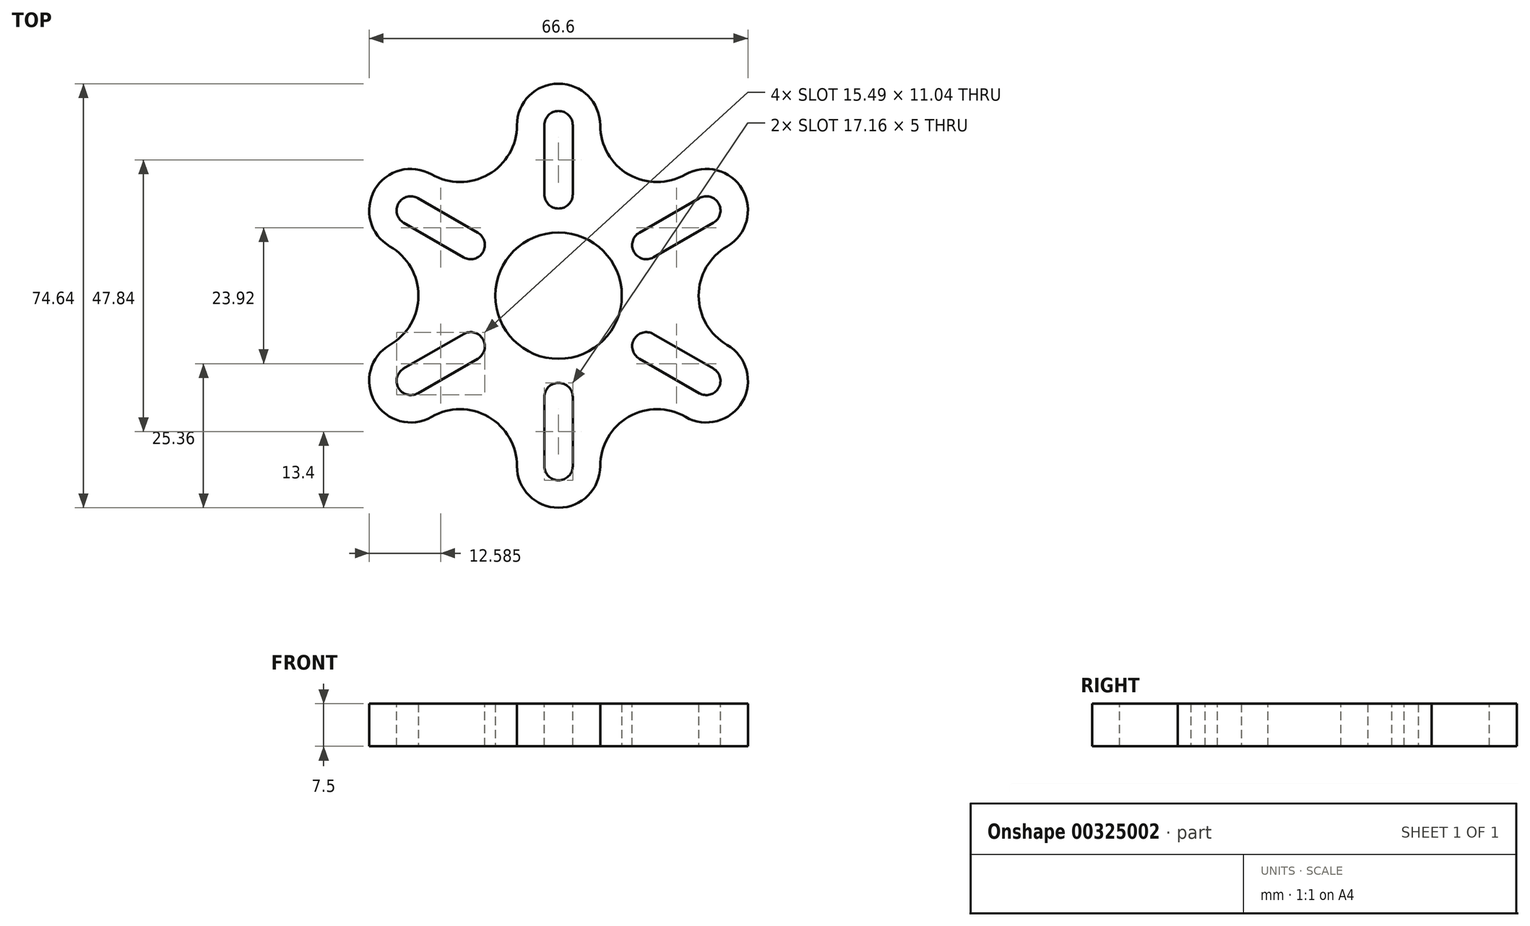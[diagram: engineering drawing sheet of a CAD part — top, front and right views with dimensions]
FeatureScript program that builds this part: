
annotation { "Feature Type Name" : "Feature", "Feature Type Description" : "" }
export const myFeature = defineFeature(function(context is Context, id is Id, definition is map)
    precondition{}
    {
        {
            var Q0;
            Q0=qCreatedBy(makeId("Top.planeOp"),FACE);
            var sketch = newSketch(context, id + "F0", { "sketchPlane" : qUnion([Q0])});
            skCircle(sketch, "E0", {"center": v(0, 0) * mm, "radius": 11.12 * mm});
            skPoint(sketch, "E1", {"position": v(0, 30) * mm});
            skCircle(sketch, "E2.cCircle", {"center": v(0, 0) * mm, "radius": 30 * mm, "construction": true});
            skLineSegment(sketch, "E2.0", {"start": v(-17.32, 30) * mm, "end": v(17.32, 30) * mm});
            skLineSegment(sketch, "E2.1", {"start": v(17.32, 30) * mm, "end": v(34.64, 0) * mm});
            skLineSegment(sketch, "E2.2", {"start": v(34.64, 0) * mm, "end": v(17.32, -30) * mm});
            skLineSegment(sketch, "E2.3", {"start": v(17.32, -30) * mm, "end": v(-17.32, -30) * mm});
            skLineSegment(sketch, "E2.4", {"start": v(-17.32, -30) * mm, "end": v(-34.64, 0) * mm});
            skLineSegment(sketch, "E2.5", {"start": v(-34.64, 0) * mm, "end": v(-17.32, 30) * mm});
            skPoint(sketch, "E3", {"position": v(-25.98, -15) * mm});
            skPoint(sketch, "E4", {"position": v(-25.98, 15) * mm});
            skPoint(sketch, "E5", {"position": v(25.98, 15) * mm});
            skPoint(sketch, "E6", {"position": v(25.98, -15) * mm});
            skCircle(sketch, "E7", {"center": v(-17.32, 30) * mm, "radius": 10 * mm});
            skCircle(sketch, "E8", {"center": v(-34.64, 0) * mm, "radius": 10 * mm});
            skCircle(sketch, "E9", {"center": v(-17.32, -30) * mm, "radius": 10 * mm});
            skCircle(sketch, "E10", {"center": v(17.32, -30) * mm, "radius": 10 * mm});
            skCircle(sketch, "E11", {"center": v(34.64, 0) * mm, "radius": 10 * mm});
            skCircle(sketch, "E12", {"center": v(17.32, 30) * mm, "radius": 10 * mm});
            skCircle(sketch, "E13", {"center": v(0, 30) * mm, "radius": 7.32 * mm});
            skCircle(sketch, "E14", {"center": v(-25.98, 15) * mm, "radius": 7.32 * mm});
            skCircle(sketch, "E15", {"center": v(-25.98, -15) * mm, "radius": 7.32 * mm});
            skCircle(sketch, "E16", {"center": v(0, -30) * mm, "radius": 7.32 * mm});
            skCircle(sketch, "E17", {"center": v(25.98, -15) * mm, "radius": 7.32 * mm});
            skCircle(sketch, "E18", {"center": v(25.98, 15) * mm, "radius": 7.32 * mm});
            skSolve(sketch);
        }
        {
            var Q0;
            Q0=makeQuery(id+"F0.imprint","IMPRINT",FACE,{"disambiguationData":[TD([[makeQuery(id+"F0.imprint","IMPRINT",EDGE,{"derivedFrom":sQuery(id+"F0.wireOp",EDGE,"E0")}),-1.0]])]});
            var Q1;
            {var subQ0=sQuery(id+"F0.wireOp",EDGE,"E13");var subQ1=sQuery(id+"F0.wireOp",EDGE,"E2.0");var subQ2=makeQuery(id+"F0.imprint","INTERSECT",VERTEX,{"derivedFrom":[subQ1,sQuery(id+"F0.wireOp",EDGE,"E7"),subQ0]});Q1=makeQuery(id+"F0.imprint","IMPRINT",FACE,{"disambiguationData":[TD([[makeQuery(id+"F0.imprint","IMPRINT",EDGE,{"disambiguationData":[TD([[subQ2,-1.0]])],"derivedFrom":subQ1}),-1.0]])]});}
            var Q2;
            {var subQ0=sQuery(id+"F0.wireOp",EDGE,"E13");var subQ1=sQuery(id+"F0.wireOp",EDGE,"E2.0");var subQ2=makeQuery(id+"F0.imprint","INTERSECT",VERTEX,{"derivedFrom":[subQ1,sQuery(id+"F0.wireOp",EDGE,"E7"),subQ0]});Q2=makeQuery(id+"F0.imprint","IMPRINT",FACE,{"disambiguationData":[TD([[makeQuery(id+"F0.imprint","IMPRINT",EDGE,{"disambiguationData":[TD([[subQ2,-1.0]])],"derivedFrom":subQ1}),1.0]])]});}
            var Q3;
            {var subQ0=sQuery(id+"F0.wireOp",EDGE,"E14");var subQ1=sQuery(id+"F0.wireOp",EDGE,"E2.5");var subQ2=makeQuery(id+"F0.imprint","INTERSECT",VERTEX,{"derivedFrom":[subQ1,sQuery(id+"F0.wireOp",EDGE,"E8"),subQ0]});Q3=makeQuery(id+"F0.imprint","IMPRINT",FACE,{"disambiguationData":[TD([[makeQuery(id+"F0.imprint","IMPRINT",EDGE,{"disambiguationData":[TD([[subQ2,-1.0]])],"derivedFrom":subQ1}),-1.0]])]});}
            var Q4;
            {var subQ0=sQuery(id+"F0.wireOp",EDGE,"E14");var subQ1=sQuery(id+"F0.wireOp",EDGE,"E2.5");var subQ2=makeQuery(id+"F0.imprint","INTERSECT",VERTEX,{"derivedFrom":[subQ1,sQuery(id+"F0.wireOp",EDGE,"E8"),subQ0]});Q4=makeQuery(id+"F0.imprint","IMPRINT",FACE,{"disambiguationData":[TD([[makeQuery(id+"F0.imprint","IMPRINT",EDGE,{"disambiguationData":[TD([[subQ2,-1.0]])],"derivedFrom":subQ1}),1.0]])]});}
            var Q5;
            {var subQ0=sQuery(id+"F0.wireOp",EDGE,"E15");var subQ1=sQuery(id+"F0.wireOp",EDGE,"E2.4");var subQ2=makeQuery(id+"F0.imprint","INTERSECT",VERTEX,{"derivedFrom":[subQ1,sQuery(id+"F0.wireOp",EDGE,"E9"),subQ0]});Q5=makeQuery(id+"F0.imprint","IMPRINT",FACE,{"disambiguationData":[TD([[makeQuery(id+"F0.imprint","IMPRINT",EDGE,{"disambiguationData":[TD([[subQ2,-1.0]])],"derivedFrom":subQ1}),-1.0]])]});}
            var Q6;
            {var subQ0=sQuery(id+"F0.wireOp",EDGE,"E15");var subQ1=sQuery(id+"F0.wireOp",EDGE,"E2.4");var subQ2=makeQuery(id+"F0.imprint","INTERSECT",VERTEX,{"derivedFrom":[subQ1,sQuery(id+"F0.wireOp",EDGE,"E9"),subQ0]});Q6=makeQuery(id+"F0.imprint","IMPRINT",FACE,{"disambiguationData":[TD([[makeQuery(id+"F0.imprint","IMPRINT",EDGE,{"disambiguationData":[TD([[subQ2,-1.0]])],"derivedFrom":subQ1}),1.0]])]});}
            var Q7;
            {var subQ0=sQuery(id+"F0.wireOp",EDGE,"E16");var subQ1=sQuery(id+"F0.wireOp",EDGE,"E2.3");var subQ2=makeQuery(id+"F0.imprint","INTERSECT",VERTEX,{"derivedFrom":[subQ1,sQuery(id+"F0.wireOp",EDGE,"E10"),subQ0]});Q7=makeQuery(id+"F0.imprint","IMPRINT",FACE,{"disambiguationData":[TD([[makeQuery(id+"F0.imprint","IMPRINT",EDGE,{"disambiguationData":[TD([[subQ2,-1.0]])],"derivedFrom":subQ1}),1.0]])]});}
            var Q8;
            {var subQ0=sQuery(id+"F0.wireOp",EDGE,"E16");var subQ1=sQuery(id+"F0.wireOp",EDGE,"E2.3");var subQ2=makeQuery(id+"F0.imprint","INTERSECT",VERTEX,{"derivedFrom":[subQ1,sQuery(id+"F0.wireOp",EDGE,"E10"),subQ0]});Q8=makeQuery(id+"F0.imprint","IMPRINT",FACE,{"disambiguationData":[TD([[makeQuery(id+"F0.imprint","IMPRINT",EDGE,{"disambiguationData":[TD([[subQ2,-1.0]])],"derivedFrom":subQ1}),-1.0]])]});}
            var Q9;
            {var subQ0=sQuery(id+"F0.wireOp",EDGE,"E17");var subQ1=sQuery(id+"F0.wireOp",EDGE,"E2.2");var subQ2=makeQuery(id+"F0.imprint","INTERSECT",VERTEX,{"derivedFrom":[subQ1,sQuery(id+"F0.wireOp",EDGE,"E11"),subQ0]});Q9=makeQuery(id+"F0.imprint","IMPRINT",FACE,{"disambiguationData":[TD([[makeQuery(id+"F0.imprint","IMPRINT",EDGE,{"disambiguationData":[TD([[subQ2,-1.0]])],"derivedFrom":subQ1}),-1.0]])]});}
            var Q10;
            {var subQ0=sQuery(id+"F0.wireOp",EDGE,"E17");var subQ1=sQuery(id+"F0.wireOp",EDGE,"E2.2");var subQ2=makeQuery(id+"F0.imprint","INTERSECT",VERTEX,{"derivedFrom":[subQ1,sQuery(id+"F0.wireOp",EDGE,"E11"),subQ0]});Q10=makeQuery(id+"F0.imprint","IMPRINT",FACE,{"disambiguationData":[TD([[makeQuery(id+"F0.imprint","IMPRINT",EDGE,{"disambiguationData":[TD([[subQ2,-1.0]])],"derivedFrom":subQ1}),1.0]])]});}
            var Q11;
            {var subQ0=sQuery(id+"F0.wireOp",EDGE,"E18");var subQ1=sQuery(id+"F0.wireOp",EDGE,"E2.1");var subQ2=makeQuery(id+"F0.imprint","INTERSECT",VERTEX,{"derivedFrom":[subQ1,sQuery(id+"F0.wireOp",EDGE,"E12"),subQ0]});Q11=makeQuery(id+"F0.imprint","IMPRINT",FACE,{"disambiguationData":[TD([[makeQuery(id+"F0.imprint","IMPRINT",EDGE,{"disambiguationData":[TD([[subQ2,-1.0]])],"derivedFrom":subQ1}),-1.0]])]});}
            var Q12;
            {var subQ0=sQuery(id+"F0.wireOp",EDGE,"E18");var subQ1=sQuery(id+"F0.wireOp",EDGE,"E2.1");var subQ2=makeQuery(id+"F0.imprint","INTERSECT",VERTEX,{"derivedFrom":[subQ1,sQuery(id+"F0.wireOp",EDGE,"E12"),subQ0]});Q12=makeQuery(id+"F0.imprint","IMPRINT",FACE,{"disambiguationData":[TD([[makeQuery(id+"F0.imprint","IMPRINT",EDGE,{"disambiguationData":[TD([[subQ2,-1.0]])],"derivedFrom":subQ1}),1.0]])]});}
            extrude(context, id + "F1", {"entities" : qUnion([Q0, Q1, Q2, Q3, Q4, Q5, Q6, Q7, Q8, Q9, Q10, Q11, Q12]), "depth" : 7.5 * mm});
        }
        {
            var Q0;
            Q0=makeQuery(id+"F1.opExtrude","CAP_FACE",FACE,{"disambiguationData":[OSD([sQuery(id+"F0.wireOp",EDGE,"E0"),sQuery(id+"F0.wireOp",EDGE,"E7"),sQuery(id+"F0.wireOp",EDGE,"E8"),sQuery(id+"F0.wireOp",EDGE,"E9"),sQuery(id+"F0.wireOp",EDGE,"E10"),sQuery(id+"F0.wireOp",EDGE,"E11"),sQuery(id+"F0.wireOp",EDGE,"E12"),sQuery(id+"F0.wireOp",EDGE,"E13"),sQuery(id+"F0.wireOp",EDGE,"E14"),sQuery(id+"F0.wireOp",EDGE,"E15"),sQuery(id+"F0.wireOp",EDGE,"E16"),sQuery(id+"F0.wireOp",EDGE,"E17"),sQuery(id+"F0.wireOp",EDGE,"E18")])],"isStart":false});
            var sketch = newSketch(context, id + "F2", { "sketchPlane" : qUnion([Q0])});
            skArc(sketch, "E19.0", {"start": v(7.32, 30) * mm, "mid": v(12.32, 21.34) * mm, "end": v(22.32, 21.34) * mm});
            skArc(sketch, "E20.0", {"start": v(-22.32, 21.34) * mm, "mid": v(-32.32, 18.66) * mm, "end": v(-29.64, 8.66) * mm});
            skArc(sketch, "E20.1", {"start": v(-22.32, 21.34) * mm, "mid": v(-12.32, 21.34) * mm, "end": v(-7.32, 30) * mm});
            skArc(sketch, "E20.2", {"start": v(7.32, 30) * mm, "mid": v(0, 37.32) * mm, "end": v(-7.32, 30) * mm});
            skArc(sketch, "E20.3", {"start": v(-29.64, -8.66) * mm, "mid": v(-24.64, 0) * mm, "end": v(-29.64, 8.66) * mm});
            skArc(sketch, "E20.4", {"start": v(-29.64, -8.66) * mm, "mid": v(-32.32, -18.66) * mm, "end": v(-22.32, -21.34) * mm});
            skArc(sketch, "E20.5", {"start": v(-7.32, -30) * mm, "mid": v(-12.32, -21.34) * mm, "end": v(-22.32, -21.34) * mm});
            skArc(sketch, "E20.6", {"start": v(-7.32, -30) * mm, "mid": v(0, -37.32) * mm, "end": v(7.32, -30) * mm});
            skArc(sketch, "E20.7", {"start": v(22.32, -21.34) * mm, "mid": v(12.32, -21.34) * mm, "end": v(7.32, -30) * mm});
            skArc(sketch, "E20.8", {"start": v(22.32, -21.34) * mm, "mid": v(32.32, -18.66) * mm, "end": v(29.64, -8.66) * mm});
            skArc(sketch, "E20.9", {"start": v(29.64, 8.66) * mm, "mid": v(24.64, 0) * mm, "end": v(29.64, -8.66) * mm});
            skArc(sketch, "E20.10", {"start": v(29.64, 8.66) * mm, "mid": v(32.32, 18.66) * mm, "end": v(22.32, 21.34) * mm});
            skCircle(sketch, "E21", {"center": v(0, 30) * mm, "radius": 2.5 * mm});
            skPoint(sketch, "E22", {"position": v(0, 17.84) * mm});
            skCircle(sketch, "E23", {"center": v(0, 17.84) * mm, "radius": 2.5 * mm});
            skLineSegment(sketch, "E24", {"start": v(-2.5, 30) * mm, "end": v(-2.5, 17.84) * mm});
            skLineSegment(sketch, "E25", {"start": v(2.5, 30) * mm, "end": v(2.5, 17.84) * mm});
            skCircle(sketch, "E26.1.0", {"center": v(-25.98, 15) * mm, "radius": 2.5 * mm});
            skLineSegment(sketch, "E26.1.1", {"start": v(-27.23, 12.83) * mm, "end": v(-16.7, 6.75) * mm});
            skLineSegment(sketch, "E26.1.2", {"start": v(-24.73, 17.17) * mm, "end": v(-14.2, 11.09) * mm});
            skCircle(sketch, "E26.1.3", {"center": v(-15.45, 8.92) * mm, "radius": 2.5 * mm});
            skCircle(sketch, "E26.2.0", {"center": v(-25.98, -15) * mm, "radius": 2.5 * mm});
            skLineSegment(sketch, "E26.2.1", {"start": v(-24.73, -17.17) * mm, "end": v(-14.2, -11.09) * mm});
            skLineSegment(sketch, "E26.2.2", {"start": v(-27.23, -12.83) * mm, "end": v(-16.7, -6.75) * mm});
            skCircle(sketch, "E26.2.3", {"center": v(-15.45, -8.92) * mm, "radius": 2.5 * mm});
            skCircle(sketch, "E26.3.0", {"center": v(0, -30) * mm, "radius": 2.5 * mm});
            skLineSegment(sketch, "E26.3.1", {"start": v(2.5, -30) * mm, "end": v(2.5, -17.84) * mm});
            skLineSegment(sketch, "E26.3.2", {"start": v(-2.5, -30) * mm, "end": v(-2.5, -17.84) * mm});
            skCircle(sketch, "E26.3.3", {"center": v(0, -17.84) * mm, "radius": 2.5 * mm});
            skCircle(sketch, "E26.4.0", {"center": v(25.98, -15) * mm, "radius": 2.5 * mm});
            skLineSegment(sketch, "E26.4.1", {"start": v(27.23, -12.83) * mm, "end": v(16.7, -6.75) * mm});
            skLineSegment(sketch, "E26.4.2", {"start": v(24.73, -17.17) * mm, "end": v(14.2, -11.09) * mm});
            skCircle(sketch, "E26.4.3", {"center": v(15.45, -8.92) * mm, "radius": 2.5 * mm});
            skCircle(sketch, "E26.5.0", {"center": v(25.98, 15) * mm, "radius": 2.5 * mm});
            skLineSegment(sketch, "E26.5.1", {"start": v(24.73, 17.17) * mm, "end": v(14.2, 11.09) * mm});
            skLineSegment(sketch, "E26.5.2", {"start": v(27.23, 12.83) * mm, "end": v(16.7, 6.75) * mm});
            skCircle(sketch, "E26.5.3", {"center": v(15.45, 8.92) * mm, "radius": 2.5 * mm});
            skPoint(sketch, "E26.center", {"position": v(0, 0) * mm});
            skSolve(sketch);
        }
        {
            var Q0;
            {var subQ0=sQuery(id+"F2.wireOp",EDGE,"E23");var subQ1=makeQuery(id+"F2.imprint","INTERSECT",VERTEX,{"derivedFrom":[subQ0,sQuery(id+"F2.wireOp",EDGE,"E24")]});Q0=makeQuery(id+"F2.imprint","IMPRINT",FACE,{"disambiguationData":[TD([[makeQuery(id+"F2.imprint","IMPRINT",EDGE,{"disambiguationData":[TD([[subQ1,1.0]])],"derivedFrom":subQ0}),1.0]])]});}
            var Q1;
            {var subQ0=sQuery(id+"F2.wireOp",EDGE,"E24");Q1=makeQuery(id+"F2.imprint","IMPRINT",FACE,{"disambiguationData":[TD([[makeQuery(id+"F2.imprint","IMPRINT",EDGE,{"derivedFrom":subQ0}),1.0]])]});}
            var Q2;
            {var subQ0=sQuery(id+"F2.wireOp",EDGE,"E21");var subQ1=makeQuery(id+"F2.imprint","INTERSECT",VERTEX,{"derivedFrom":[subQ0,sQuery(id+"F2.wireOp",EDGE,"E24")]});Q2=makeQuery(id+"F2.imprint","IMPRINT",FACE,{"disambiguationData":[TD([[makeQuery(id+"F2.imprint","IMPRINT",EDGE,{"disambiguationData":[TD([[subQ1,1.0]])],"derivedFrom":subQ0}),1.0]])]});}
            var Q3;
            {var subQ0=sQuery(id+"F2.wireOp",EDGE,"E26.1.1");Q3=makeQuery(id+"F2.imprint","IMPRINT",FACE,{"disambiguationData":[TD([[makeQuery(id+"F2.imprint","IMPRINT",EDGE,{"derivedFrom":subQ0}),1.0]])]});}
            var Q4;
            {var subQ0=sQuery(id+"F2.wireOp",EDGE,"E26.1.3");var subQ1=makeQuery(id+"F2.imprint","INTERSECT",VERTEX,{"derivedFrom":[sQuery(id+"F2.wireOp",EDGE,"E26.1.1"),subQ0]});Q4=makeQuery(id+"F2.imprint","IMPRINT",FACE,{"disambiguationData":[TD([[makeQuery(id+"F2.imprint","IMPRINT",EDGE,{"disambiguationData":[TD([[subQ1,1.0]])],"derivedFrom":subQ0}),1.0]])]});}
            var Q5;
            {var subQ0=sQuery(id+"F2.wireOp",EDGE,"E26.1.0");var subQ1=makeQuery(id+"F2.imprint","INTERSECT",VERTEX,{"derivedFrom":[subQ0,sQuery(id+"F2.wireOp",EDGE,"E26.1.1")]});Q5=makeQuery(id+"F2.imprint","IMPRINT",FACE,{"disambiguationData":[TD([[makeQuery(id+"F2.imprint","IMPRINT",EDGE,{"disambiguationData":[TD([[subQ1,1.0]])],"derivedFrom":subQ0}),1.0]])]});}
            var Q6;
            {var subQ0=sQuery(id+"F2.wireOp",EDGE,"E26.2.1");Q6=makeQuery(id+"F2.imprint","IMPRINT",FACE,{"disambiguationData":[TD([[makeQuery(id+"F2.imprint","IMPRINT",EDGE,{"derivedFrom":subQ0}),1.0]])]});}
            var Q7;
            {var subQ0=sQuery(id+"F2.wireOp",EDGE,"E26.2.3");var subQ1=makeQuery(id+"F2.imprint","INTERSECT",VERTEX,{"derivedFrom":[sQuery(id+"F2.wireOp",EDGE,"E26.2.1"),subQ0]});Q7=makeQuery(id+"F2.imprint","IMPRINT",FACE,{"disambiguationData":[TD([[makeQuery(id+"F2.imprint","IMPRINT",EDGE,{"disambiguationData":[TD([[subQ1,1.0]])],"derivedFrom":subQ0}),1.0]])]});}
            var Q8;
            {var subQ0=sQuery(id+"F2.wireOp",EDGE,"E26.2.0");var subQ1=makeQuery(id+"F2.imprint","INTERSECT",VERTEX,{"derivedFrom":[subQ0,sQuery(id+"F2.wireOp",EDGE,"E26.2.1")]});Q8=makeQuery(id+"F2.imprint","IMPRINT",FACE,{"disambiguationData":[TD([[makeQuery(id+"F2.imprint","IMPRINT",EDGE,{"disambiguationData":[TD([[subQ1,1.0]])],"derivedFrom":subQ0}),1.0]])]});}
            var Q9;
            {var subQ0=sQuery(id+"F2.wireOp",EDGE,"E26.3.1");Q9=makeQuery(id+"F2.imprint","IMPRINT",FACE,{"disambiguationData":[TD([[makeQuery(id+"F2.imprint","IMPRINT",EDGE,{"derivedFrom":subQ0}),1.0]])]});}
            var Q10;
            {var subQ0=sQuery(id+"F2.wireOp",EDGE,"E26.3.3");var subQ1=makeQuery(id+"F2.imprint","INTERSECT",VERTEX,{"derivedFrom":[sQuery(id+"F2.wireOp",EDGE,"E26.3.1"),subQ0]});Q10=makeQuery(id+"F2.imprint","IMPRINT",FACE,{"disambiguationData":[TD([[makeQuery(id+"F2.imprint","IMPRINT",EDGE,{"disambiguationData":[TD([[subQ1,1.0]])],"derivedFrom":subQ0}),1.0]])]});}
            var Q11;
            {var subQ0=sQuery(id+"F2.wireOp",EDGE,"E26.3.0");var subQ1=makeQuery(id+"F2.imprint","INTERSECT",VERTEX,{"derivedFrom":[subQ0,sQuery(id+"F2.wireOp",EDGE,"E26.3.1")]});Q11=makeQuery(id+"F2.imprint","IMPRINT",FACE,{"disambiguationData":[TD([[makeQuery(id+"F2.imprint","IMPRINT",EDGE,{"disambiguationData":[TD([[subQ1,1.0]])],"derivedFrom":subQ0}),1.0]])]});}
            var Q12;
            {var subQ0=sQuery(id+"F2.wireOp",EDGE,"E26.4.1");Q12=makeQuery(id+"F2.imprint","IMPRINT",FACE,{"disambiguationData":[TD([[makeQuery(id+"F2.imprint","IMPRINT",EDGE,{"derivedFrom":subQ0}),1.0]])]});}
            var Q13;
            {var subQ0=sQuery(id+"F2.wireOp",EDGE,"E26.4.3");var subQ1=makeQuery(id+"F2.imprint","INTERSECT",VERTEX,{"derivedFrom":[sQuery(id+"F2.wireOp",EDGE,"E26.4.1"),subQ0]});Q13=makeQuery(id+"F2.imprint","IMPRINT",FACE,{"disambiguationData":[TD([[makeQuery(id+"F2.imprint","IMPRINT",EDGE,{"disambiguationData":[TD([[subQ1,1.0]])],"derivedFrom":subQ0}),1.0]])]});}
            var Q14;
            {var subQ0=sQuery(id+"F2.wireOp",EDGE,"E26.4.0");var subQ1=makeQuery(id+"F2.imprint","INTERSECT",VERTEX,{"derivedFrom":[subQ0,sQuery(id+"F2.wireOp",EDGE,"E26.4.1")]});Q14=makeQuery(id+"F2.imprint","IMPRINT",FACE,{"disambiguationData":[TD([[makeQuery(id+"F2.imprint","IMPRINT",EDGE,{"disambiguationData":[TD([[subQ1,1.0]])],"derivedFrom":subQ0}),1.0]])]});}
            var Q15;
            {var subQ0=sQuery(id+"F2.wireOp",EDGE,"E26.5.1");Q15=makeQuery(id+"F2.imprint","IMPRINT",FACE,{"disambiguationData":[TD([[makeQuery(id+"F2.imprint","IMPRINT",EDGE,{"derivedFrom":subQ0}),1.0]])]});}
            var Q16;
            {var subQ0=sQuery(id+"F2.wireOp",EDGE,"E26.5.3");var subQ1=makeQuery(id+"F2.imprint","INTERSECT",VERTEX,{"derivedFrom":[sQuery(id+"F2.wireOp",EDGE,"E26.5.1"),subQ0]});Q16=makeQuery(id+"F2.imprint","IMPRINT",FACE,{"disambiguationData":[TD([[makeQuery(id+"F2.imprint","IMPRINT",EDGE,{"disambiguationData":[TD([[subQ1,1.0]])],"derivedFrom":subQ0}),1.0]])]});}
            var Q17;
            {var subQ0=sQuery(id+"F2.wireOp",EDGE,"E26.5.0");var subQ1=makeQuery(id+"F2.imprint","INTERSECT",VERTEX,{"derivedFrom":[subQ0,sQuery(id+"F2.wireOp",EDGE,"E26.5.1")]});Q17=makeQuery(id+"F2.imprint","IMPRINT",FACE,{"disambiguationData":[TD([[makeQuery(id+"F2.imprint","IMPRINT",EDGE,{"disambiguationData":[TD([[subQ1,1.0]])],"derivedFrom":subQ0}),1.0]])]});}
            extrude(context, id + "F3", {"entities" : qUnion([Q0, Q1, Q2, Q3, Q4, Q5, Q6, Q7, Q8, Q9, Q10, Q11, Q12, Q13, Q14, Q15, Q16, Q17]), "operationType" : NewBodyOperationType.REMOVE, "oppositeDirection" : true, "depth" : 25 * mm});
        }
    });
